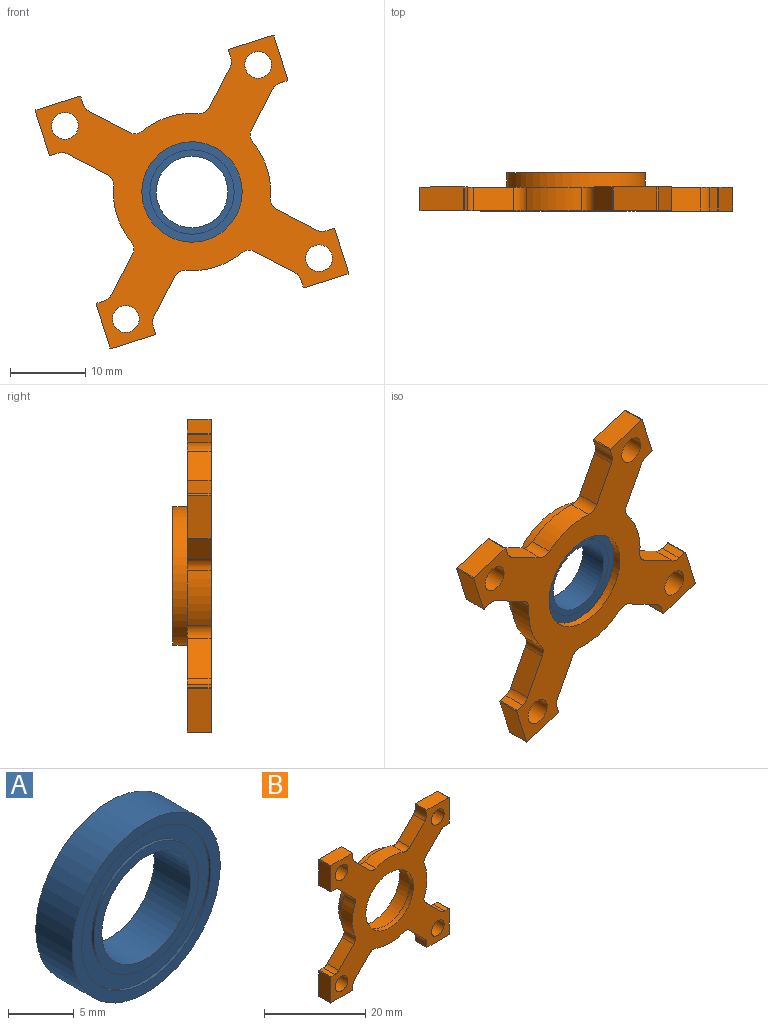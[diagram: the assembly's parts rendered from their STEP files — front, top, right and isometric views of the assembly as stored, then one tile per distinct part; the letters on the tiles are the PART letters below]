
ASSEMBLY  parts=2 mates=1
PART A: 12 faces, bbox 15.9x3.9x15.9 mm
  f0: cylinder r=5.6mm len=11.2mm, axis (0,-1,0), area 8.9mm2, adj f6,f11
  f1: cylinder r=6.93mm len=13.87mm, axis (0,-1,0), area 11.1mm2, adj f9,f11
  f2: cylinder r=5.6mm len=11.2mm, axis (0,1,0), area 8.9mm2, adj f7,f10
  f3: cylinder r=6.93mm len=13.87mm, axis (0,1,0), area 11.1mm2, adj f8,f10
  f4: cylinder r=4.76mm len=9.53mm, axis (0,-1,0), area 117mm2, adj f6,f7
  f5: cylinder r=7.94mm len=15.88mm, axis (0,-1,0), area 195.1mm2, adj f8,f9
  f6: plane 11.2x11.2mm, normal (0,-1,0), area 27.3mm2, adj f0,f4
  f7: plane 11.2x11.2mm, normal (0,1,0), area 27.3mm2, adj f2,f4
  f8: plane 15.88x15.88mm, normal (0,1,0), area 46.9mm2, adj f3,f5
  f9: plane 15.88x15.88mm, normal (0,-1,0), area 46.9mm2, adj f1,f5
  f10: plane 13.87x13.87mm, normal (0,1,0), area 52.5mm2, adj f2,f3
  f11: plane 13.87x13.87mm, normal (0,-1,0), area 52.5mm2, adj f0,f1
PART B: 67 faces, bbox 33.3x5.1x33.3 mm
  f0: cylinder r=6.67mm len=13.34mm, axis (0,1,0), area 46.8mm2, adj f38,f66
  f1: cylinder r=7.94mm len=15.88mm, axis (0,-1,0), area 197.6mm2, adj f65,f66
  f2: cylinder r=9.21mm len=18.42mm, axis (0,-1,0), area 110.2mm2, adj f10,f65
  f3: cylinder r=1.59mm len=3.18mm, axis (0,-1,0), area 5.9mm2, adj f10,f23,f24,f38
  f4: cylinder r=1.59mm len=3.18mm, axis (0,-1,0), area 5.9mm2, adj f10,f22,f23,f38
  f5: cylinder r=1.78mm len=3.56mm, axis (0,1,0), area 35.5mm2, adj f10,f38
  f6: cylinder r=1.78mm len=3.56mm, axis (0,1,0), area 35.5mm2, adj f10,f38
  f7: cylinder r=1.78mm len=3.56mm, axis (0,1,0), area 35.5mm2, adj f10,f38
  f8: cylinder r=1.78mm len=3.56mm, axis (0,1,0), area 35.5mm2, adj f10,f38
  f9: cylinder r=10.46mm len=7.74mm, axis (0,-1,0), area 25.2mm2, adj f10,f38,f61,f62
  f10: plane 33.27x33.27mm, normal (0,1,0), area 349.3mm2, adj f2,f3,f4,f5,f6,f7,f8,f9
  f11: plane 3.18x1.08mm, normal (1,0,0), area 3.4mm2, adj f10,f38,f48,f54
  f12: plane 6.1x3.18mm, normal (0,0,-1), area 19.4mm2, adj f10,f38,f48,f49
  f13: plane 6.1x3.18mm, normal (-1,0,0), area 19.4mm2, adj f10,f38,f49,f50
  f14: plane 3.18x1.08mm, normal (0,0,1), area 3.4mm2, adj f10,f38,f50,f53
  f15: plane 4.24x4.24mm, normal (-0.71,0,0.71), area 19mm2, adj f10,f38,f53,f63
  f16: cylinder r=10.46mm len=7.74mm, axis (0,-1,0), area 25.2mm2, adj f10,f38,f63,f64
  f17: plane 4.24x4.24mm, normal (-0.71,0,-0.71), area 19mm2, adj f10,f38,f52,f64
  f18: plane 3.18x1.08mm, normal (0,0,-1), area 3.4mm2, adj f10,f38,f39,f52
  f19: plane 6.1x3.18mm, normal (-1,0,0), area 19.4mm2, adj f10,f38,f39,f40
  f20: plane 6.1x3.18mm, normal (0,0,1), area 19.4mm2, adj f10,f38,f40,f43
  f21: plane 3.18x1.08mm, normal (1,0,0), area 3.4mm2, adj f10,f38,f43,f51
  f22: plane 4.24x4.24mm, normal (0.71,0,0.71), area 19mm2, adj f4,f10,f38,f51
  f23: cylinder r=10.46mm len=7.74mm, axis (0,-1,0), area 25.2mm2, adj f3,f4,f10,f38
  f24: plane 4.24x4.24mm, normal (-0.71,0,0.71), area 19mm2, adj f3,f10,f38,f58
  f25: plane 3.18x1.08mm, normal (-1,0,0), area 3.4mm2, adj f10,f38,f41,f58
  f26: plane 6.1x3.18mm, normal (0,0,1), area 19.4mm2, adj f10,f38,f41,f44
  f27: plane 6.1x3.18mm, normal (1,0,0), area 19.4mm2, adj f10,f38,f44,f45
  f28: plane 3.18x1.08mm, normal (0,0,-1), area 3.4mm2, adj f10,f38,f45,f57
  f29: plane 4.24x4.24mm, normal (0.71,0,-0.71), area 19mm2, adj f10,f38,f57,f59
  f30: cylinder r=10.46mm len=7.74mm, axis (0,-1,0), area 25.2mm2, adj f10,f38,f59,f60
  f31: plane 4.24x4.24mm, normal (0.71,0,0.71), area 19mm2, adj f10,f38,f56,f60
  f32: plane 3.18x1.08mm, normal (0,0,1), area 3.4mm2, adj f10,f38,f46,f56
  f33: plane 6.1x3.18mm, normal (1,0,0), area 19.4mm2, adj f10,f38,f46,f47
  f34: plane 6.1x3.18mm, normal (0,0,-1), area 19.4mm2, adj f10,f38,f42,f47
  f35: plane 3.18x1.08mm, normal (-1,0,0), area 3.4mm2, adj f10,f38,f42,f55
  f36: plane 4.24x4.24mm, normal (-0.71,0,-0.71), area 19mm2, adj f10,f38,f55,f62
  f37: plane 4.24x4.24mm, normal (0.71,0,-0.71), area 19mm2, adj f10,f38,f54,f61
  f38: plane 33.27x33.27mm, normal (0,-1,0), area 476mm2, adj f0,f3,f4,f5,f6,f7,f8,f9
  f39: cylinder r=0.13mm len=3.18mm, axis (0,-1,0), area 0.6mm2, adj f10,f18,f19,f38
  f40: cylinder r=0.13mm len=3.18mm, axis (0,1,0), area 0.6mm2, adj f10,f19,f20,f38
  f41: cylinder r=0.13mm len=3.18mm, axis (0,1,0), area 0.6mm2, adj f10,f25,f26,f38
  f42: cylinder r=0.13mm len=3.18mm, axis (0,1,0), area 0.6mm2, adj f10,f34,f35,f38
  f43: cylinder r=0.13mm len=3.18mm, axis (0,-1,0), area 0.6mm2, adj f10,f20,f21,f38
  f44: cylinder r=0.13mm len=3.18mm, axis (0,-1,0), area 0.6mm2, adj f10,f26,f27,f38
  f45: cylinder r=0.13mm len=3.18mm, axis (0,-1,0), area 0.6mm2, adj f10,f27,f28,f38
  f46: cylinder r=0.13mm len=3.18mm, axis (0,-1,0), area 0.6mm2, adj f10,f32,f33,f38
  f47: cylinder r=0.13mm len=3.18mm, axis (0,-1,0), area 0.6mm2, adj f10,f33,f34,f38
  f48: cylinder r=0.13mm len=3.18mm, axis (0,-1,0), area 0.6mm2, adj f10,f11,f12,f38
  f49: cylinder r=0.13mm len=3.18mm, axis (0,-1,0), area 0.6mm2, adj f10,f12,f13,f38
  f50: cylinder r=0.13mm len=3.18mm, axis (0,1,0), area 0.6mm2, adj f10,f13,f14,f38
  f51: cylinder r=1.59mm len=3.18mm, axis (0,-1,0), area 4mm2, adj f10,f21,f22,f38
  f52: cylinder r=1.59mm len=3.18mm, axis (0,-1,0), area 4mm2, adj f10,f17,f18,f38
  f53: cylinder r=1.59mm len=3.18mm, axis (0,-1,0), area 4mm2, adj f10,f14,f15,f38
  f54: cylinder r=1.59mm len=3.18mm, axis (0,-1,0), area 4mm2, adj f10,f11,f37,f38
  f55: cylinder r=1.59mm len=3.18mm, axis (0,-1,0), area 4mm2, adj f10,f35,f36,f38
  f56: cylinder r=1.59mm len=3.18mm, axis (0,-1,0), area 4mm2, adj f10,f31,f32,f38
  f57: cylinder r=1.59mm len=3.18mm, axis (0,-1,0), area 4mm2, adj f10,f28,f29,f38
  f58: cylinder r=1.59mm len=3.18mm, axis (0,-1,0), area 4mm2, adj f10,f24,f25,f38
  f59: cylinder r=1.59mm len=3.18mm, axis (0,-1,0), area 5.9mm2, adj f10,f29,f30,f38
  f60: cylinder r=1.59mm len=3.18mm, axis (0,-1,0), area 5.9mm2, adj f10,f30,f31,f38
  f61: cylinder r=1.59mm len=3.18mm, axis (0,-1,0), area 5.9mm2, adj f9,f10,f37,f38
  f62: cylinder r=1.59mm len=3.18mm, axis (0,-1,0), area 5.9mm2, adj f9,f10,f36,f38
  f63: cylinder r=1.59mm len=3.18mm, axis (0,-1,0), area 5.9mm2, adj f10,f15,f16,f38
  f64: cylinder r=1.59mm len=3.18mm, axis (0,-1,0), area 5.9mm2, adj f10,f16,f17,f38
  f65: plane 18.42x18.42mm, normal (0,1,0), area 68.4mm2, adj f1,f2
  f66: plane 15.88x15.88mm, normal (0,1,0), area 58.3mm2, adj f0,f1
PLACE A rot(axis=(0,-1,0),17.5deg) t=(8.63,15.12,26.91)mm
PLACE B rot(axis=(0,-1,0),17.5deg) t=(8.63,14.01,26.91)mm
MATE fastened B.f0 <-> A.f0  axis (0,1,0) through (8.63,19.09,26.91)mm
